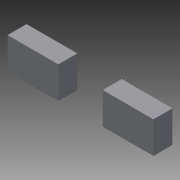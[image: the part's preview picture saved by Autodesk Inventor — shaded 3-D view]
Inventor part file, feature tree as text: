
AUTODESK INVENTOR PART (.ipt)
format: ipt  version: 2013 (Build 170138000, 138)  size: 75,264 bytes
history: native  units: in
note: dims shown in document units (in); Inventor stores cm internally (conversion verified against a paired STEP export)
features: extrude x1, sketch x1
ambient origin geometry x8: Origin, YZ Plane, XZ Plane, XY Plane, X Axis, Y Axis, Z Axis, Center Point
bodies: Solid1 (feature_tree)
feature tree (2):
  extrude  "Extrusion1"  Depth=5.0in
  sketch  "Sketch1"  dims[d0=8.0in d1=5.0in d2=23.0in d3=5.0in d4=8.0in d5=5.0in d6=3.0in d7=0.0in]
